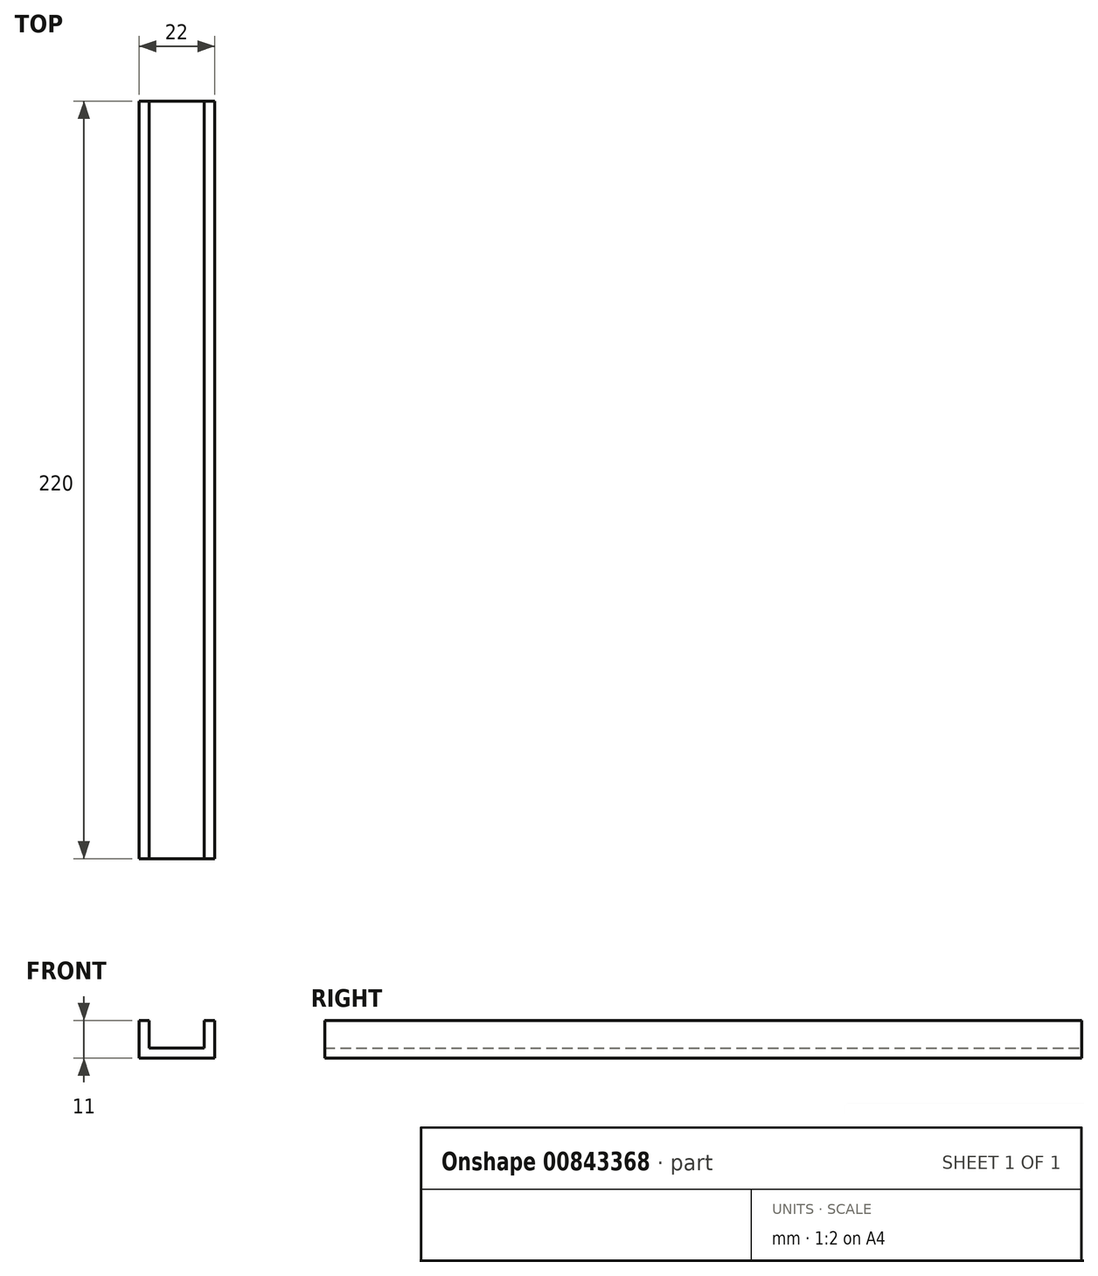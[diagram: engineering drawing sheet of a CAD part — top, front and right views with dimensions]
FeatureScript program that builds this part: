
annotation { "Feature Type Name" : "Feature", "Feature Type Description" : "" }
export const myFeature = defineFeature(function(context is Context, id is Id, definition is map)
    precondition{}
    {
        {
            var Q0;
            Q0=qCreatedBy(makeId("Front.planeOp"),FACE);
            var sketch = newSketch(context, id + "F0", { "sketchPlane" : qUnion([Q0])});
            skLineSegment(sketch, "E0.top", {"start": v(-6.1, -6.3) * mm, "end": v(15.9, -6.3) * mm});
            skLineSegment(sketch, "E0.left", {"start": v(-6.1, 4.7) * mm, "end": v(-6.1, -6.3) * mm});
            skLineSegment(sketch, "E0.right", {"start": v(15.9, 4.7) * mm, "end": v(15.9, -6.3) * mm});
            skPoint(sketch, "E1", {"position": v(15.9, -3.3) * mm});
            skPoint(sketch, "E2", {"position": v(-6.1, -3.3) * mm});
            skLineSegment(sketch, "E3", {"start": v(-3.1, 4.7) * mm, "end": v(-3.1, -6.3) * mm});
            skLineSegment(sketch, "E4", {"start": v(-6.1, -3.3) * mm, "end": v(15.9, -3.3) * mm});
            skLineSegment(sketch, "E5", {"start": v(12.9, 4.7) * mm, "end": v(12.9, -6.3) * mm});
            skPoint(sketch, "E6", {"position": v(-3.1, -3.3) * mm});
            skPoint(sketch, "E7", {"position": v(12.9, -3.3) * mm});
            skPoint(sketch, "E8", {"position": v(-3.1, 4.7) * mm});
            skPoint(sketch, "E9", {"position": v(12.9, 4.7) * mm});
            skPoint(sketch, "E10", {"position": v(15.9, 4.7) * mm});
            skPoint(sketch, "E11", {"position": v(-6.1, 4.7) * mm});
            skPoint(sketch, "E12", {"position": v(-6.1, -6.3) * mm});
            skPoint(sketch, "E13", {"position": v(-3.1, -6.3) * mm});
            skPoint(sketch, "E14", {"position": v(12.9, -6.3) * mm});
            skPoint(sketch, "E15", {"position": v(15.9, -6.3) * mm});
            skLineSegment(sketch, "E16", {"start": v(-6.1, 4.7) * mm, "end": v(-3.1, 4.7) * mm});
            skLineSegment(sketch, "E17", {"start": v(12.9, 4.7) * mm, "end": v(15.9, 4.7) * mm});
            skSolve(sketch);
        }
        {
            var Q0;
            Q0 = qSketchRegion(id + "F0", true);
            extrude(context, id + "F1", {"entities" : qUnion([Q0]), "depth" : 220 * mm, "offsetDistance" : 25 * mm});
        }
    });
